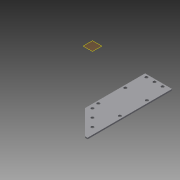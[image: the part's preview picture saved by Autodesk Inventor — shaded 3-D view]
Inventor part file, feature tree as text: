
AUTODESK INVENTOR PART (.ipt)
format: ipt  version: 2013 (Build 170138000, 138)  size: 105,984 bytes
history: native  units: in
note: dims shown in document units (in); Inventor stores cm internally (conversion verified against a paired STEP export)
features: sketch x1, plane x1, extrude x1
ambient origin geometry x8: Origin, YZ Plane, XZ Plane, XY Plane, X Axis, Y Axis, Z Axis, Center Point
bodies: Solid1 (feature_tree)
feature tree (3):
  sketch  "Sketch1"  dims[d34=12.0in d36=16.0in d38=45.0deg d40=0.266in d41=0.266in d42=0.266in d43=0.266in d44=0.25in d45=0.25in d46=0.25in d48=0.25in d49=0.25in d50=0.25in d51=0.25in d52=0.25in d53=157.5deg d58=0.266in d59=0.266in d64=0.266in d70=0.266in d72=2.5in d73=0.125in d74=0.0in]
  plane  "Work Plane1"
  extrude  "Extrusion5"  Depth=16.0in
